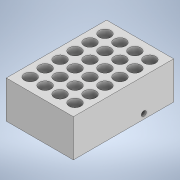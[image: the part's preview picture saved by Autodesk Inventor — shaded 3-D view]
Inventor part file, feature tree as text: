
AUTODESK INVENTOR PART (.ipt)
format: ipt  version: 2020 (Build 240168000, 168)  size: 202,752 bytes
history: native  units: in
note: dims shown in document units (in); Inventor stores cm internally (conversion verified against a paired STEP export)
features: sketch x6, hole x5, extrude x1, pattern_linear x1
ambient origin geometry x8: Origin, YZ Plane, XZ Plane, XY Plane, X Axis, Y Axis, Z Axis, Center Point
bodies: Solid1 (feature_tree)
feature tree (13):
  extrude  "Extrusion1"  Depth=5.0299in
  hole  "Hole1"  [1 undecoded]
  hole  "Hole2"  [1 undecoded]
  pattern_linear  "Rectangular Pattern1"  Spacing1=1.878in  [1 undecoded]
  hole  "Hole3"  [1 undecoded]
  hole  "Hole4"  [1 undecoded]
  hole  "Hole5"  [1 undecoded]
  sketch  "Sketch1"  dims[d0=3.3654in d1=5.0299in]
  sketch  "Sketch2"  dims[d2=1.0in d3=135.0deg]
  sketch  "Sketch4"  dims[d4=1.0in d5=1.0in]
  sketch  "Sketch5"  dims[d6=135.0deg]
  sketch  "Sketch6"  dims[d7=1.0in]
  sketch  "Sketch7"  dims[d8=45.0deg d9=1.878in d10=0.0in d11=1.0in d12=135.0deg d13=1.0in d14=135.0deg d15=1.0in d16=45.0deg d17=1.0in d18=45.0deg d19=0.145in d20=0.25in d21=0.375in d22=0.19in d23=0.5635in d24=0.375in d25=0.8108in d28=0.5906in d29=0.25in d30=0.375in d31=0.25in d32=0.5635in d33=1.378in d34=0.0in d35=1.5748in d37=0.75in d38=2.3622in d40=0.75in d41=0.5575in d42=0.64in d43=1.5in d44=0.25in d45=0.25in d46=0.25in d47=0.119in d48=0.25in d49=0.5635in d50=1.25in d51=0.8108in d52=0.25in d53=0.125in d54=0.25in d55=0.119in d56=0.25in d57=0.5635in d58=2.0in d59=0.8108in d60=1.5in d61=0.25in d62=0.25in d63=0.25in d64=0.119in d65=0.25in d66=0.5635in d67=1.25in d68=0.8108in]
note: 6 required parameter values undecoded (feature->parameter linkage not recoverable at this tier; creation-order binding heuristic only, values carry confidence <= 0.55)
